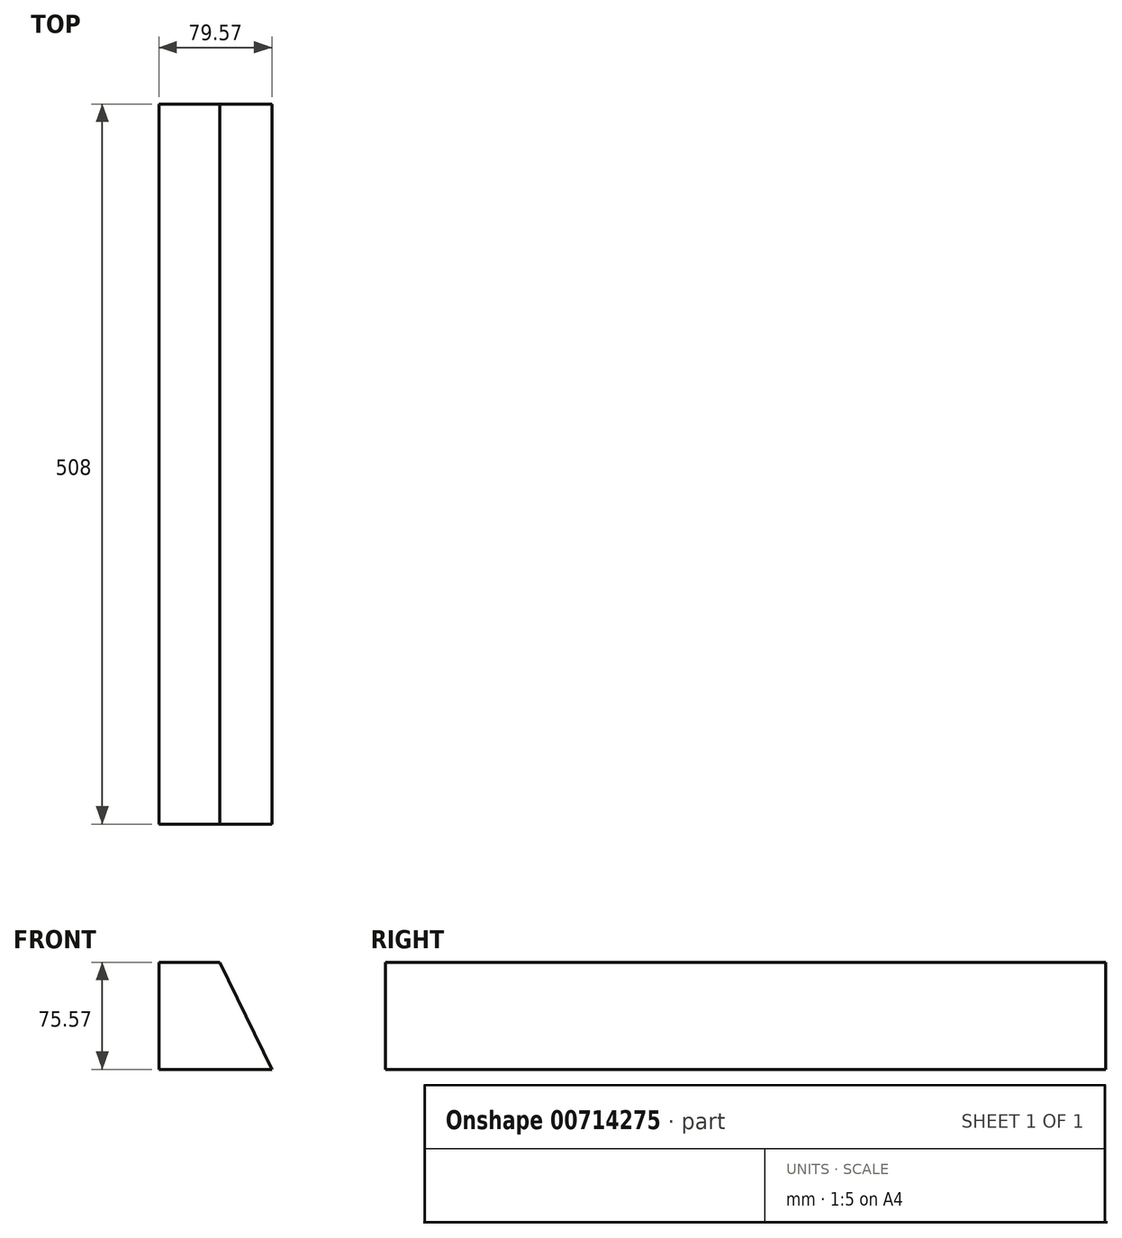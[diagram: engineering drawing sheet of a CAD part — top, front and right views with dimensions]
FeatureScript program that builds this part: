
annotation { "Feature Type Name" : "Feature", "Feature Type Description" : "" }
export const myFeature = defineFeature(function(context is Context, id is Id, definition is map)
    precondition{}
    {
        {
            var Q0;
            Q0=qCreatedBy(makeId("Front.planeOp"),FACE);
            var sketch = newSketch(context, id + "F0", { "sketchPlane" : qUnion([Q0])});
            skLineSegment(sketch, "E0", {"start": v(0, 41.55) * mm, "end": v(42.74, 41.55) * mm});
            skLineSegment(sketch, "E1", {"start": v(42.74, 41.55) * mm, "end": v(79.57, -34.02) * mm});
            skLineSegment(sketch, "E2", {"start": v(79.57, -34.02) * mm, "end": v(0, -34.02) * mm});
            skLineSegment(sketch, "E3", {"start": v(0, -34.02) * mm, "end": v(0, 41.55) * mm});
            skSolve(sketch);
        }
        {
            var Q0;
            Q0=makeQuery(id+"F0.imprint","IMPRINT",FACE,{"disambiguationData":[TD([[makeQuery(id+"F0.imprint","IMPRINT",EDGE,{"derivedFrom":sQuery(id+"F0.wireOp",EDGE,"E0")}),-1.0]])]});
            extrude(context, id + "F1", {"entities" : qUnion([Q0]), "depth" : 508 * mm, "offsetDistance" : 25.4 * mm});
        }
    });
